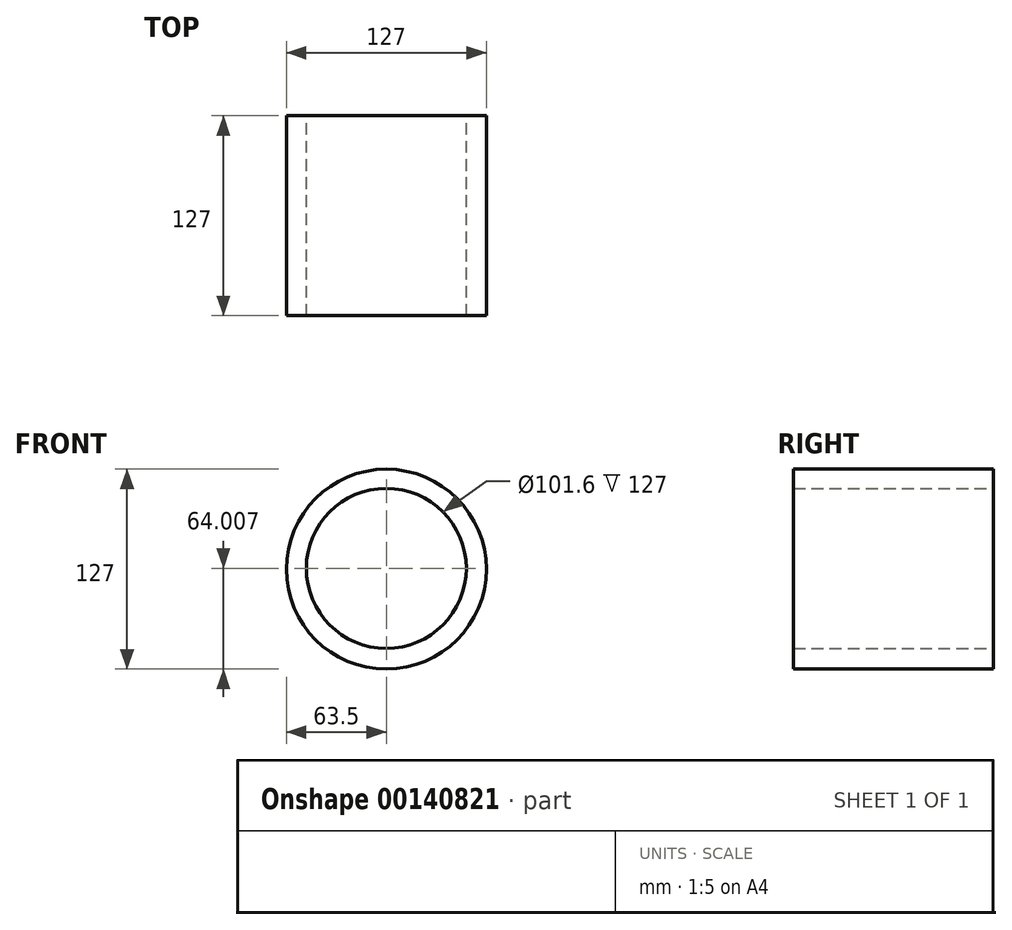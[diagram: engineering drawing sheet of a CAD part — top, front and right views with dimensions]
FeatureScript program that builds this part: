
annotation { "Feature Type Name" : "Feature", "Feature Type Description" : "" }
export const myFeature = defineFeature(function(context is Context, id is Id, definition is map)
    precondition{}
    {
        {
            var Q0;
            Q0=qCreatedBy(makeId("Front.planeOp"),FACE);
            var sketch = newSketch(context, id + "F0", { "sketchPlane" : qUnion([Q0])});
            skCircle(sketch, "E0", {"center": v(0, 0) * mm, "radius": 63.5 * mm});
            skCircle(sketch, "E1", {"center": v(0, 0.5) * mm, "radius": 50.8 * mm});
            skSolve(sketch);
        }
        {
            var Q0;
            Q0=makeQuery(id+"F0.imprint","IMPRINT",FACE,{"disambiguationData":[TD([[makeQuery(id+"F0.imprint","IMPRINT",EDGE,{"derivedFrom":sQuery(id+"F0.wireOp",EDGE,"E0")}),1.0]])]});
            extrude(context, id + "F1", {"entities" : qUnion([Q0]), "endBound" : BoundingType.SYMMETRIC, "depth" : 127 * mm});
        }
    });
